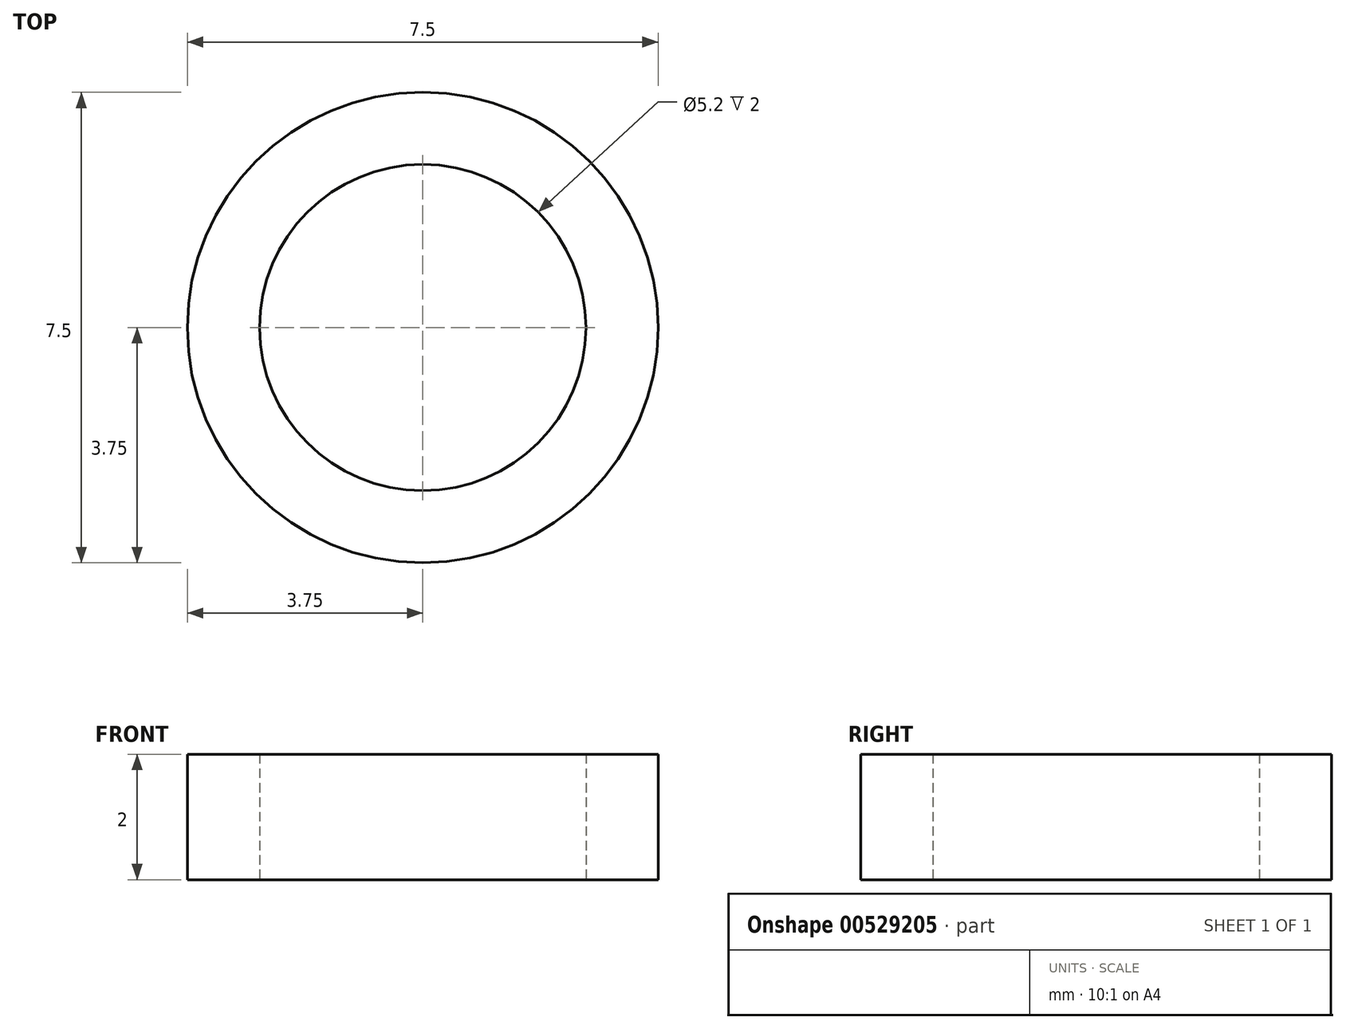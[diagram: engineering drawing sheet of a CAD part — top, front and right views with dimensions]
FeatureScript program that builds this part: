
annotation { "Feature Type Name" : "Feature", "Feature Type Description" : "" }
export const myFeature = defineFeature(function(context is Context, id is Id, definition is map)
    precondition{}
    {
        {
            var Q0;
            Q0=qCreatedBy(makeId("Top.planeOp"),FACE);
            var sketch = newSketch(context, id + "F0", { "sketchPlane" : qUnion([Q0])});
            skCircle(sketch, "E0", {"center": v(0, 0) * mm, "radius": 2.6 * mm});
            skCircle(sketch, "E1", {"center": v(0, 0) * mm, "radius": 3.75 * mm});
            skSolve(sketch);
        }
        {
            var Q0;
            Q0=makeQuery(id+"F0.imprint","IMPRINT",FACE,{"disambiguationData":[TD([[makeQuery(id+"F0.imprint","IMPRINT",EDGE,{"derivedFrom":sQuery(id+"F0.wireOp",EDGE,"E0")}),-1.0]])]});
            extrude(context, id + "F1", {"entities" : qUnion([Q0]), "depth" : 2 * mm, "offsetDistance" : 25 * mm});
        }
    });
